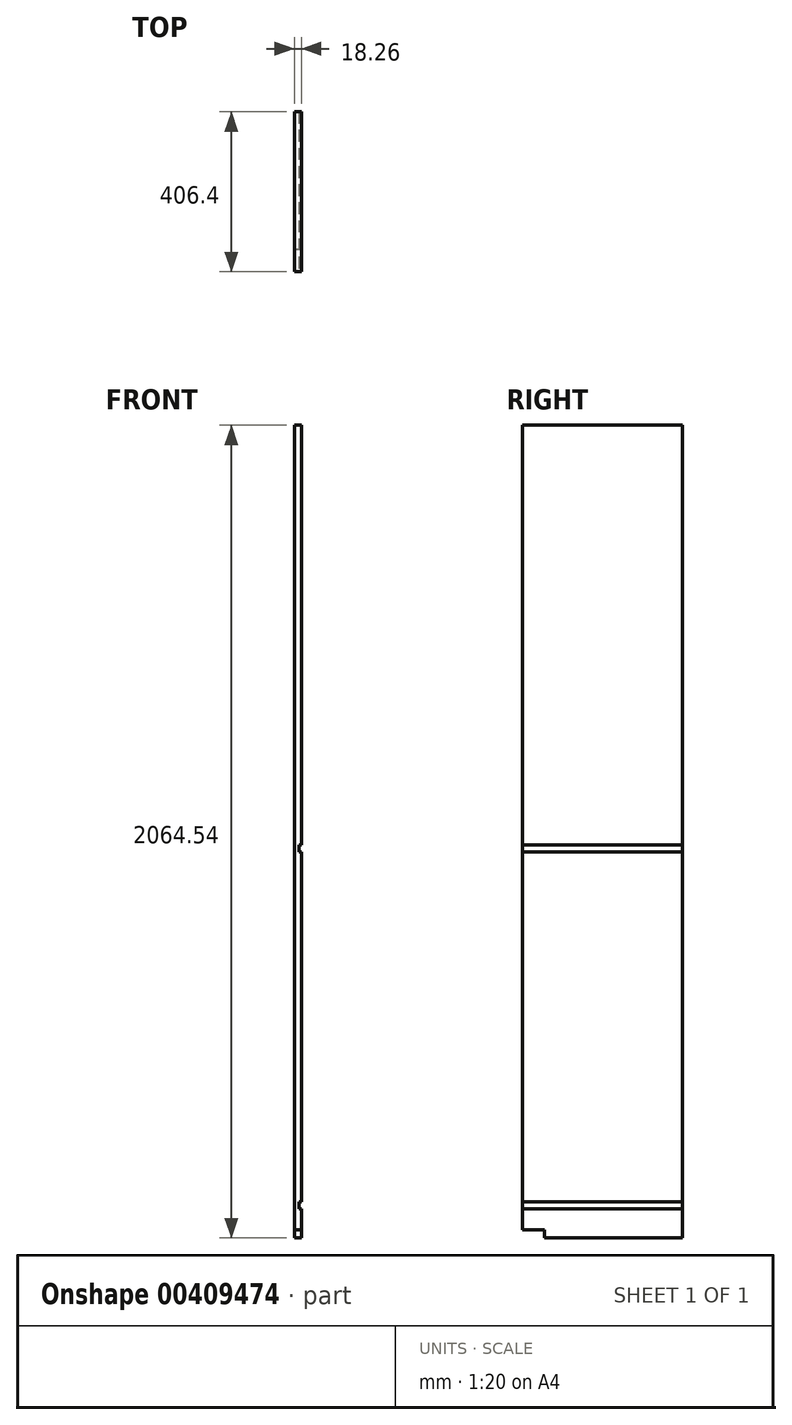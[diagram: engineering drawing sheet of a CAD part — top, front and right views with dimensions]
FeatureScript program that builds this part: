
annotation { "Feature Type Name" : "Feature", "Feature Type Description" : "" }
export const myFeature = defineFeature(function(context is Context, id is Id, definition is map)
    precondition{}
    {
        {
            var Q0;
            Q0=qCreatedBy(makeId("Front.planeOp"),FACE);
            var sketch = newSketch(context, id + "F0", { "sketchPlane" : qUnion([Q0])});
            skLineSegment(sketch, "E0.bottom", {"start": v(0, 0) * mm, "end": v(18.26, 0) * mm});
            skLineSegment(sketch, "E0.top", {"start": v(0, 2064.54) * mm, "end": v(18.26, 2064.54) * mm});
            skLineSegment(sketch, "E0.left", {"start": v(0, 0) * mm, "end": v(0, 2064.54) * mm});
            skLineSegment(sketch, "E0.right", {"start": v(18.26, 0) * mm, "end": v(18.26, 2064.54) * mm});
            skSolve(sketch);
        }
        {
            var Q0;
            Q0 = qSketchRegion(id + "F0", true);
            extrude(context, id + "F1", {"entities" : qUnion([Q0]), "depth" : 406.4 * mm});
        }
        {
            var Q0;
            Q0=makeQuery(id+"F1.opExtrude","CAP_FACE",FACE,{"disambiguationData":[OSD([sQuery(id+"F0.wireOp",EDGE,"E0.bottom"),sQuery(id+"F0.wireOp",EDGE,"E0.top"),sQuery(id+"F0.wireOp",EDGE,"E0.left"),sQuery(id+"F0.wireOp",EDGE,"E0.right")])],"isStart":false});
            var sketch = newSketch(context, id + "F2", { "sketchPlane" : qUnion([Q0])});
            skLineSegment(sketch, "E1", {"start": v(18.26, 73.03) * mm, "end": v(18.26, 91.29) * mm});
            skLineSegment(sketch, "E2", {"start": v(18.26, 980.28) * mm, "end": v(18.26, 995.8) * mm});
            skLineSegment(sketch, "E3.bottom", {"start": v(18.26, 998.54) * mm, "end": v(11.9, 998.54) * mm});
            skLineSegment(sketch, "E3.top", {"start": v(18.26, 980.28) * mm, "end": v(11.9, 980.28) * mm});
            skLineSegment(sketch, "E3.left", {"start": v(18.26, 995.8) * mm, "end": v(18.26, 980.28) * mm});
            skLineSegment(sketch, "E4.bottom", {"start": v(18.26, 73.03) * mm, "end": v(11.9, 73.03) * mm});
            skLineSegment(sketch, "E4.top", {"start": v(18.26, 91.3) * mm, "end": v(11.9, 91.3) * mm});
            skLineSegment(sketch, "E4.left", {"start": v(18.26, 73.03) * mm, "end": v(18.26, 91.3) * mm});
            skLineSegment(sketch, "E4.right", {"start": v(11.9, 73.03) * mm, "end": v(11.9, 91.3) * mm});
            skLineSegment(sketch, "E5.right", {"start": v(11.9, 980.28) * mm, "end": v(11.9, 998.54) * mm});
            skLineSegment(sketch, "E6", {"start": v(18.26, 998.54) * mm, "end": v(18.26, 995.8) * mm});
            skSolve(sketch);
        }
        {
            var Q0;
            Q0 = qSketchRegion(id + "F2", true);
            extrude(context, id + "F3", {"entities" : qUnion([Q0]), "operationType" : NewBodyOperationType.REMOVE, "oppositeDirection" : true, "depth" : 406.4 * mm});
        }
        {
            var Q0;
            Q0=makeQuery(id+"F1.opExtrude","SWEPT_FACE",FACE,{"disambiguationData":[OSD([sQuery(id+"F0.wireOp",EDGE,"E0.left")])]});
            var sketch = newSketch(context, id + "F4", { "sketchPlane" : qUnion([Q0])});
            skLineSegment(sketch, "E7.bottom", {"start": v(406.4, 0) * mm, "end": v(350.52, 0) * mm});
            skLineSegment(sketch, "E7.top", {"start": v(406.4, 19.69) * mm, "end": v(350.52, 19.69) * mm});
            skLineSegment(sketch, "E7.left", {"start": v(406.4, 0) * mm, "end": v(406.4, 19.69) * mm});
            skLineSegment(sketch, "E7.right", {"start": v(350.52, 0) * mm, "end": v(350.52, 19.68) * mm});
            skSolve(sketch);
        }
        {
            var Q0;
            Q0=makeQuery(id+"F4.imprint","IMPRINT",FACE,{"disambiguationData":[TD([[makeQuery(id+"F4.imprint","IMPRINT",EDGE,{"derivedFrom":sQuery(id+"F4.wireOp",EDGE,"E7.bottom")}),-1.0]])]});
            extrude(context, id + "F5", {"entities" : qUnion([Q0]), "operationType" : NewBodyOperationType.REMOVE, "oppositeDirection" : true, "depth" : 25.4 * mm});
        }
    });
